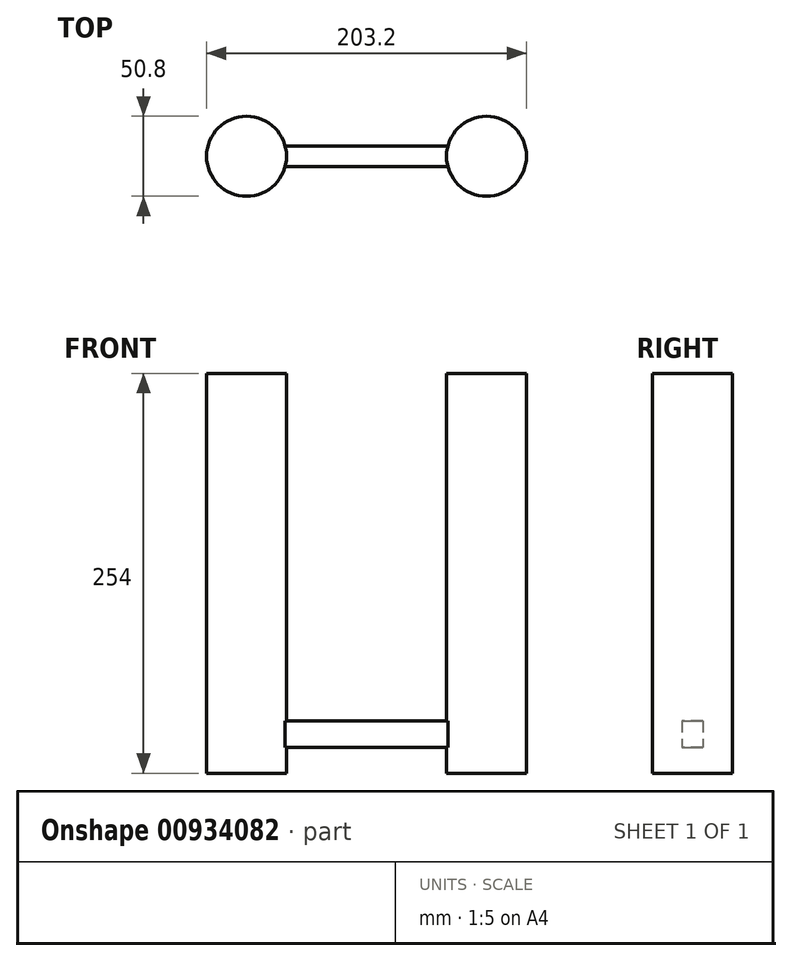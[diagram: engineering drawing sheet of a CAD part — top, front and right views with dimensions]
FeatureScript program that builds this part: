
annotation { "Feature Type Name" : "Feature", "Feature Type Description" : "" }
export const myFeature = defineFeature(function(context is Context, id is Id, definition is map)
    precondition{}
    {
        {
            var Q0;
            Q0=qCreatedBy(makeId("Top.planeOp"),FACE);
            var sketch = newSketch(context, id + "F0", { "sketchPlane" : qUnion([Q0])});
            skLineSegment(sketch, "E0", {"start": v(-92.78, 0) * mm, "end": v(88.02, 0) * mm, "construction": true});
            skCircle(sketch, "E1", {"center": v(-76.2, 0) * mm, "radius": 25.4 * mm});
            skCircle(sketch, "E2.MirrorC", {"center": v(76.2, 0) * mm, "radius": 25.4 * mm});
            skSolve(sketch);
        }
        {
            var Q0;
            Q0=qCreatedBy(makeId("Right.planeOp"),FACE);
            var sketch = newSketch(context, id + "F1", { "sketchPlane" : qUnion([Q0])});
            skLineSegment(sketch, "E3.bottom", {"start": v(-6.54, 33.33) * mm, "end": v(6.54, 33.33) * mm});
            skLineSegment(sketch, "E3.top", {"start": v(-6.54, 16.45) * mm, "end": v(6.54, 16.45) * mm});
            skLineSegment(sketch, "E3.left", {"start": v(-6.54, 33.33) * mm, "end": v(-6.54, 16.45) * mm});
            skLineSegment(sketch, "E3.right", {"start": v(6.54, 33.33) * mm, "end": v(6.54, 16.45) * mm});
            skSolve(sketch);
        }
        {
            var Q0;
            Q0 = qSketchRegion(id + "F1", true);
            extrude(context, id + "F2", {"entities" : qUnion([Q0]), "endBound" : BoundingType.SYMMETRIC, "depth" : 152.4 * mm, "offsetDistance" : 25.4 * mm});
        }
        {
            var Q0;
            Q0 = qSketchRegion(id + "F0", true);
            extrude(context, id + "F3", {"entities" : qUnion([Q0]), "operationType" : NewBodyOperationType.ADD, "depth" : 254 * mm, "offsetDistance" : 25.4 * mm});
        }
    });
